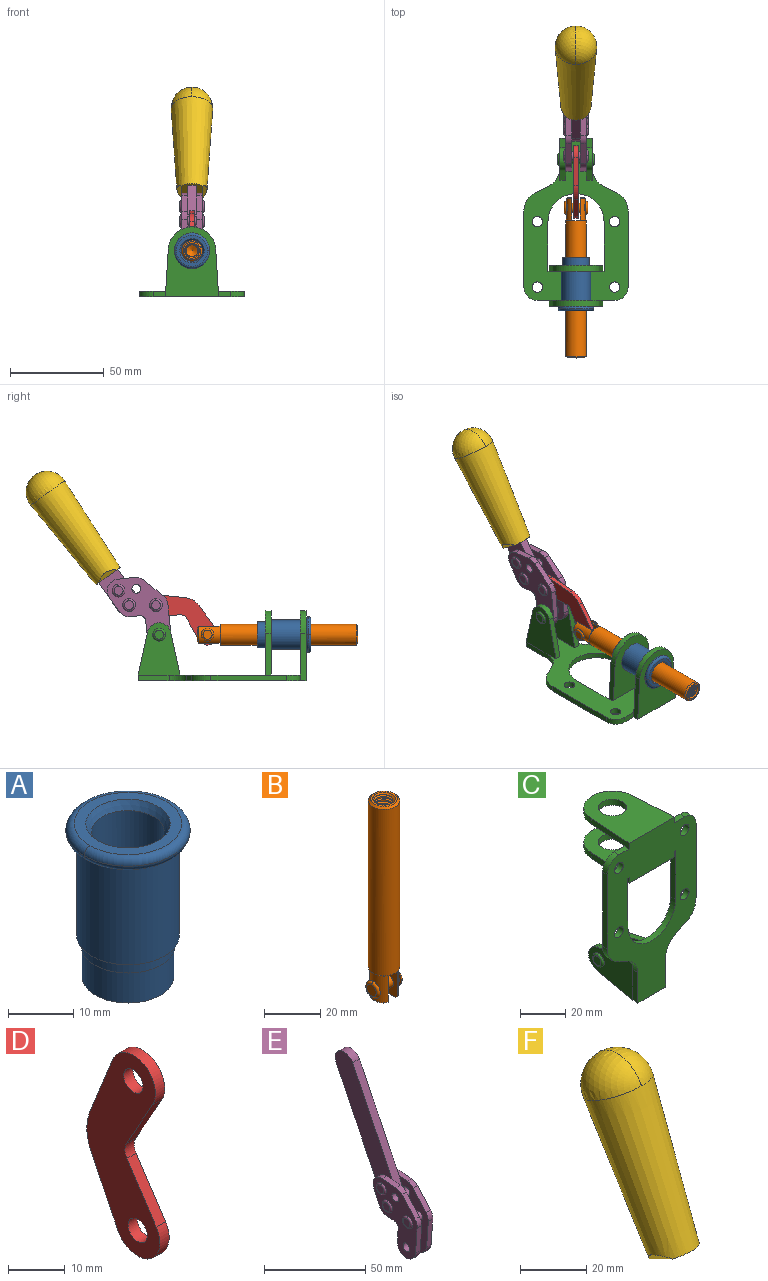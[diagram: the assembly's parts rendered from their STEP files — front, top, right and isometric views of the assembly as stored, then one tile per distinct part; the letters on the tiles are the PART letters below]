
ASSEMBLY  parts=6 mates=6
PART A: 15 faces, bbox 20.6x20.6x28.7 mm
  f0: torus R=8.26mm, axis (0,0,1), area 56.8mm2, adj f1,f10,f12
  f1: torus R=8.26mm, axis (0,0,1), area 56.8mm2, adj f0,f6,f13
  f2: cylinder r=5.59mm len=25.91mm, axis (0,0,1), area 909.6mm2, adj f3,f4
  f3: cone r=6.86mm half-angle=45deg, axis (0,0,-1), area 70.2mm2, adj f2,f14
  f4: cone r=6.47mm half-angle=30deg, axis (0,0,1), area 66.7mm2, adj f2,f13
  f5: cylinder r=7.04mm len=14.07mm, axis (0,0,1), area 252.6mm2, adj f11,f14
  f6: torus R=8.26mm, axis (0,0,1), area 56.8mm2, adj f1,f12,f13
  f7: cylinder r=7.16mm len=14.33mm, axis (0,0,1), area 91.5mm2, adj f9,f11
  f8: cylinder r=7.86mm len=18.42mm, axis (0,0,1), area 909.6mm2, adj f9,f10
  f9: plane 15.72x15.72mm, normal (0,0,-1), area 33mm2, adj f7,f8
  f10: plane 16.51x16.51mm, normal (0,0,-1), area 19.9mm2, adj f0,f8,f12
  f11: plane 14.33x14.33mm, normal (0,0,-1), area 5.7mm2, adj f5,f7
  f12: torus R=8.26mm, axis (0,0,1), area 56.8mm2, adj f0,f6,f10
  f13: plane 16.51x16.51mm, normal (0,0,1), area 82.7mm2, adj f1,f4,f6
  f14: plane 14.07x14.07mm, normal (0,0,-1), area 7.8mm2, adj f3,f5
PART B: 48 faces, bbox 12.6x11.1x86.1 mm
  f0: torus R=2.41mm, axis (-1,0,0), area 15mm2, adj f30,f32,f34
  f1: torus R=2.41mm, axis (-1,0,0), area 15mm2, adj f29,f31,f33
  f2: cylinder r=5.54mm len=72.39mm, axis (0,0,1), area 2518.5mm2, adj f3,f4,f42,f43
  f3: cone r=5.54mm half-angle=45deg, axis (0,0,1), area 7.6mm2, adj f2,f5,f41
  f4: cone r=5.54mm half-angle=45deg, axis (0,0,-1), area 34.9mm2, adj f2,f39
  f5: cylinder r=5.08mm len=11.48mm, axis (0,0,1), area 108.3mm2, adj f3,f7,f8,f41
  f6: cylinder r=2.41mm len=4.83mm, axis (-1,0,0), area 71.2mm2, adj f40,f41
  f7: cylinder r=2.41mm len=4.83mm, axis (-1,0,0), area 7.6mm2, adj f5,f34
  f8: cone r=5.08mm half-angle=45deg, axis (0,0,1), area 10.6mm2, adj f5,f37,f41
  f9: cone r=3.98mm half-angle=45deg, axis (0,0,1), area 17.6mm2, adj f27,f39,f45,f46,f47
  f10: cylinder r=2.41mm len=4.83mm, axis (-1,0,0), area 7.6mm2, adj f33,f38
  f11: cylinder r=3.2mm len=6.4mm, axis (0,0,1), area 78.4mm2, adj f12,f28,f44,f45,f47
  f12: cylinder r=3.2mm len=6.4mm, axis (0,0,1), area 10.5mm2, adj f11,f13,f45,f47
  f13: cylinder r=3.2mm len=6.4mm, axis (0,0,1), area 10.5mm2, adj f12,f14,f45,f47
  f14: cylinder r=3.2mm len=6.4mm, axis (0,0,1), area 10.5mm2, adj f13,f15,f45,f47
  f15: cylinder r=3.2mm len=6.4mm, axis (0,0,1), area 10.5mm2, adj f14,f16,f45,f47
  f16: cylinder r=3.2mm len=6.4mm, axis (0,0,1), area 10.5mm2, adj f15,f17,f45,f47
  f17: cylinder r=3.2mm len=6.4mm, axis (0,0,1), area 10.5mm2, adj f16,f18,f45,f47
  f18: cylinder r=3.2mm len=6.4mm, axis (0,0,1), area 10.5mm2, adj f17,f19,f45,f47
  f19: cylinder r=3.2mm len=6.4mm, axis (0,0,1), area 10.5mm2, adj f18,f20,f45,f47
  f20: cylinder r=3.2mm len=6.4mm, axis (0,0,1), area 10.5mm2, adj f19,f21,f45,f47
  f21: cylinder r=3.2mm len=6.4mm, axis (0,0,1), area 10.5mm2, adj f20,f22,f45,f47
  f22: cylinder r=3.2mm len=6.4mm, axis (0,0,1), area 10.5mm2, adj f21,f23,f45,f47
  f23: cylinder r=3.2mm len=6.4mm, axis (0,0,1), area 10.5mm2, adj f22,f24,f45,f47
  f24: cylinder r=3.2mm len=6.4mm, axis (0,0,1), area 10.5mm2, adj f23,f25,f45,f47
  f25: cylinder r=3.2mm len=6.4mm, axis (0,0,1), area 10.5mm2, adj f24,f26,f45,f47
  f26: cylinder r=3.2mm len=6.4mm, axis (0,0,1), area 10.5mm2, adj f25,f27,f45,f47
  f27: cylinder r=3.2mm len=6.4mm, axis (0,0,1), area 7.4mm2, adj f9,f26,f45,f47
  f28: cone r=3.2mm half-angle=60deg, axis (0,0,1), area 37.2mm2, adj f11
  f29: plane 4.83x4.83mm, normal (-1,0,0), area 18.3mm2, adj f1,f31
  f30: plane 4.83x4.83mm, normal (1,0,0), area 18.3mm2, adj f0,f32
  f31: torus R=2.41mm, axis (-1,0,0), area 15mm2, adj f1,f29,f33
  f32: torus R=2.41mm, axis (-1,0,0), area 15mm2, adj f0,f30,f34
  f33: plane 6.83x6.83mm, normal (1,0,0), area 18.3mm2, adj f1,f10,f31
  f34: plane 6.83x6.83mm, normal (-1,0,0), area 18.3mm2, adj f0,f7,f32
  f35: cone r=5.08mm half-angle=45deg, axis (0,0,1), area 10.6mm2, adj f36,f38,f40
  f36: plane 7.25x1.97mm, normal (0,0,-1), area 10mm2, adj f35,f40
  f37: plane 7.25x1.97mm, normal (0,0,-1), area 10mm2, adj f8,f41
  f38: cylinder r=5.08mm len=11.48mm, axis (0,0,1), area 108.3mm2, adj f10,f35,f40,f42
  f39: plane 9.55x9.55mm, normal (0,0,1), area 22mm2, adj f4,f9
  f40: plane 12.76x10.09mm, normal (1,0,0), area 95.7mm2, adj f6,f35,f36,f38,f42,f43
  f41: plane 12.76x10.09mm, normal (-1,0,0), area 95.7mm2, adj f3,f5,f6,f8,f37,f43
  f42: cone r=5.54mm half-angle=45deg, axis (0,0,1), area 7.6mm2, adj f2,f38,f40
  f43: plane 11.07x4.7mm, normal (0,0,-1), area 50.4mm2, adj f2,f40,f41
  f44: plane 0.89x0.62mm, normal (-1,0,0), area 0.3mm2, adj f11,f45,f46,f47
  f45: bspline ~24.8x7.63mm, area 266.6mm2, adj f9,f11,f12,f13,f14,f15,f16,f17
  f46: bspline ~24.87x7.63mm, area 73.6mm2, adj f9,f44,f45,f47
  f47: bspline ~24.98x7.63mm, area 272.5mm2, adj f9,f11,f12,f13,f14,f15,f16,f17
PART C: 55 faces, bbox 55.7x37.4x89.8 mm
  f0: torus R=2.41mm, axis (-1,0,0), area 15mm2, adj f11,f15,f25
  f1: torus R=2.41mm, axis (-1,0,0), area 15mm2, adj f10,f12,f22
  f2: cylinder r=2.78mm len=5.56mm, axis (0,-1,0), area 54.2mm2, adj f30,f54
  f3: cylinder r=14.99mm len=29.97mm, axis (0,-1,0), area 145.9mm2, adj f30,f49,f53,f54
  f4: cylinder r=2.78mm len=5.56mm, axis (0,-1,0), area 54.2mm2, adj f30,f54
  f5: cylinder r=2.78mm len=5.56mm, axis (0,-1,0), area 54.2mm2, adj f30,f54
  f6: cylinder r=2.78mm len=5.56mm, axis (0,-1,0), area 54.2mm2, adj f30,f54
  f7: cylinder r=6.35mm len=12.7mm, axis (0,0,1), area 123.6mm2, adj f27,f51
  f8: cylinder r=6.35mm len=12.7mm, axis (0,0,-1), area 124.7mm2, adj f21,f35
  f9: cylinder r=2.41mm len=11.18mm, axis (-1,0,0), area 169.4mm2, adj f16,f19
  f10: plane 4.83x4.83mm, normal (1,0,0), area 18.3mm2, adj f1,f12
  f11: plane 4.83x4.83mm, normal (-1,0,0), area 18.3mm2, adj f0,f15
  f12: torus R=2.41mm, axis (-1,0,0), area 15mm2, adj f1,f10,f22
  f13: cylinder r=6.35mm len=12.41mm, axis (1,0,0), area 53.4mm2, adj f18,f19,f22,f23
  f14: cylinder r=6.35mm len=12.41mm, axis (-1,0,0), area 53.4mm2, adj f16,f17,f24,f25
  f15: torus R=2.41mm, axis (-1,0,0), area 15mm2, adj f0,f11,f25
  f16: plane 27.86x22.35mm, normal (1,0,0), area 425.4mm2, adj f9,f14,f17,f24,f30
  f17: plane 22.86x4.97mm, normal (0,0.21,0.98), area 72.5mm2, adj f14,f16,f25,f30
  f18: plane 22.86x4.97mm, normal (0,0.21,0.98), area 72.5mm2, adj f13,f19,f22,f30
  f19: plane 27.86x22.35mm, normal (-1,0,0), area 425.4mm2, adj f9,f13,f18,f23,f30
  f20: cylinder r=12.7mm len=25.35mm, axis (0,0,-1), area 119.8mm2, adj f21,f34,f35,f36
  f21: plane 34.21x28.07mm, normal (0,0,-1), area 702.4mm2, adj f8,f20,f30,f34,f36
  f22: plane 27.96x22.45mm, normal (1,0,0), area 407.2mm2, adj f1,f12,f13,f18,f23,f30,f42,f43
  f23: plane 22.86x4.97mm, normal (0,0.21,-0.98), area 72.5mm2, adj f13,f19,f22,f44
  f24: plane 22.86x4.97mm, normal (0,0.21,-0.98), area 72.5mm2, adj f14,f16,f25,f44
  f25: plane 27.86x22.35mm, normal (-1,0,0), area 407.1mm2, adj f0,f14,f15,f17,f24,f30,f45,f46
  f26: plane 3.1x0.95mm, normal (0,0,-1), area 2.7mm2, adj f30,f49,f50,f54
  f27: plane 34.21x28.07mm, normal (0,0,1), area 702.4mm2, adj f7,f28,f30,f50,f52
  f28: cylinder r=12.7mm len=25.35mm, axis (0,0,1), area 118.8mm2, adj f27,f50,f51,f52
  f29: plane 3.1x0.95mm, normal (0,0,-1), area 2.7mm2, adj f30,f52,f53,f54
  f30: plane 86.54x55.63mm, normal (0,1,0), area 2362.9mm2, adj f2,f3,f4,f5,f6,f16,f17,f18
  f31: plane 40.56x3.1mm, normal (-1,0,0), area 125.7mm2, adj f30,f32,f48,f54
  f32: cylinder r=7.11mm len=7.11mm, axis (0,-1,0), area 34.6mm2, adj f30,f31,f33,f54
  f33: plane 6.67x3.1mm, normal (0,0,1), area 20.4mm2, adj f30,f32,f34,f54
  f34: plane 25.39x3.13mm, normal (-1,0.06,0), area 79.5mm2, adj f20,f21,f33,f35,f54
  f35: plane 37.31x28.45mm, normal (0,0,1), area 789.9mm2, adj f8,f20,f34,f36,f54
  f36: plane 25.39x3.13mm, normal (1,0.06,0), area 79.5mm2, adj f20,f21,f35,f37,f54
  f37: plane 6.67x3.1mm, normal (0,0,1), area 20.4mm2, adj f30,f36,f38,f54
  f38: cylinder r=7.11mm len=7.11mm, axis (0,-1,0), area 34.6mm2, adj f30,f37,f39,f54
  f39: plane 40.56x3.1mm, normal (1,0,0), area 125.7mm2, adj f30,f38,f40,f54
  f40: cylinder r=11.18mm len=10.16mm, axis (0,-1,0), area 39.5mm2, adj f30,f39,f41,f54
  f41: plane 6.09x3.1mm, normal (0.42,0,-0.91), area 20.8mm2, adj f30,f40,f42,f54
  f42: cylinder r=11.18mm len=9.41mm, axis (0,-1,0), area 37.2mm2, adj f22,f30,f41,f43,f54
  f43: plane 16.5x3.1mm, normal (1,0,0), area 51.1mm2, adj f22,f42,f44,f54
  f44: plane 17.37x3.1mm, normal (0,0,-1), area 53.8mm2, adj f23,f24,f30,f43,f45,f54
  f45: plane 16.5x3.1mm, normal (-1,0,0), area 51.1mm2, adj f25,f44,f46,f54
  f46: cylinder r=11.18mm len=9.41mm, axis (0,-1,0), area 37.2mm2, adj f25,f30,f45,f47,f54
  f47: plane 6.09x3.1mm, normal (-0.42,0,-0.91), area 20.8mm2, adj f30,f46,f48,f54
  f48: cylinder r=11.18mm len=10.16mm, axis (0,-1,0), area 39.5mm2, adj f30,f31,f47,f54
  f49: plane 26.54x3.1mm, normal (-1,0,0), area 82.3mm2, adj f3,f26,f30,f54
  f50: plane 25.39x3.1mm, normal (1,0.06,0), area 78.8mm2, adj f26,f27,f28,f51,f54
  f51: plane 37.31x28.45mm, normal (0,0,-1), area 789.9mm2, adj f7,f28,f50,f52,f54
  f52: plane 25.39x3.1mm, normal (-1,0.06,0), area 78.8mm2, adj f27,f28,f29,f51,f54
  f53: plane 26.54x3.1mm, normal (1,0,0), area 82.3mm2, adj f3,f29,f30,f54
  f54: plane 89.66x55.63mm, normal (0,-1,0), area 2678.5mm2, adj f2,f3,f4,f5,f6,f26,f29,f31
PART D: 12 faces, bbox 2.3x18.2x42.8 mm
  f0: cylinder r=2.4mm len=4.8mm, axis (1,0,0), area 34.9mm2, adj f4,f11
  f1: cylinder r=10.41mm len=8.47mm, axis (1,0,0), area 20.2mm2, adj f4,f9,f10,f11
  f2: cylinder r=3.05mm len=3.16mm, axis (1,0,0), area 7.7mm2, adj f4,f6,f7,f11
  f3: cylinder r=2.4mm len=4.8mm, axis (1,0,0), area 34.9mm2, adj f4,f11
  f4: plane 42.81x18.23mm, normal (-1,0,0), area 414.1mm2, adj f0,f1,f2,f3,f5,f6,f7,f8
  f5: cylinder r=5.54mm len=10.67mm, axis (1,0,0), area 41.8mm2, adj f4,f6,f10,f11
  f6: plane 11.66x6.53mm, normal (0,-0.87,-0.49), area 30.9mm2, adj f2,f4,f5,f11
  f7: plane 11.17x7.33mm, normal (0,-0.84,0.55), area 30.9mm2, adj f2,f4,f8,f11
  f8: cylinder r=5.54mm len=10.51mm, axis (1,0,0), area 41.8mm2, adj f4,f7,f9,f11
  f9: plane 13.67x6.67mm, normal (0,0.9,-0.44), area 35.1mm2, adj f1,f4,f8,f11
  f10: plane 14.1x5.7mm, normal (0,0.93,0.37), area 35.1mm2, adj f1,f4,f5,f11
  f11: plane 42.81x18.23mm, normal (1,0,0), area 414.1mm2, adj f0,f1,f2,f3,f5,f6,f7,f8
PART E: 59 faces, bbox 12.9x60.2x99.6 mm
  f0: torus R=2.39mm, axis (-1,0,0), area 14.9mm2, adj f20,f43,f51
  f1: torus R=2.39mm, axis (-1,0,0), area 14.9mm2, adj f19,f42,f51
  f2: torus R=2.39mm, axis (-1,0,0), area 14.9mm2, adj f18,f35,f51
  f3: torus R=2.39mm, axis (-1,0,0), area 14.9mm2, adj f14,f17,f23
  f4: torus R=2.39mm, axis (-1,0,0), area 14.9mm2, adj f13,f16,f23
  f5: torus R=2.39mm, axis (-1,0,0), area 14.9mm2, adj f12,f15,f23
  f6: cylinder r=2.39mm len=4.78mm, axis (1,0,0), area 46.5mm2, adj f48,f50,f51
  f7: cylinder r=2.39mm len=4.78mm, axis (1,0,0), area 46.5mm2, adj f50,f51
  f8: cylinder r=6.35mm len=12.68mm, axis (1,0,0), area 61.8mm2, adj f38,f39,f50,f51
  f9: cylinder r=2.39mm len=4.78mm, axis (-1,0,0), area 70.5mm2, adj f46,f50
  f10: cylinder r=2.39mm len=4.78mm, axis (-1,0,0), area 46.5mm2, adj f23,f45,f46
  f11: cylinder r=2.39mm len=4.78mm, axis (-1,0,0), area 46.5mm2, adj f23,f46
  f12: plane 4.78x4.78mm, normal (1,0,0), area 17.9mm2, adj f5,f15
  f13: plane 4.78x4.78mm, normal (1,0,0), area 17.9mm2, adj f4,f16
  f14: plane 4.78x4.78mm, normal (1,0,0), area 17.9mm2, adj f3,f17
  f15: torus R=2.39mm, axis (-1,0,0), area 14.9mm2, adj f5,f12,f23
  f16: torus R=2.39mm, axis (-1,0,0), area 14.9mm2, adj f4,f13,f23
  f17: torus R=2.39mm, axis (-1,0,0), area 14.9mm2, adj f3,f14,f23
  f18: plane 4.78x4.78mm, normal (-1,0,0), area 17.9mm2, adj f2,f35
  f19: plane 4.78x4.78mm, normal (-1,0,0), area 17.9mm2, adj f1,f42
  f20: plane 4.78x4.78mm, normal (-1,0,0), area 17.9mm2, adj f0,f43
  f21: plane 2.26x0.2mm, normal (1,0,0), area 0.2mm2, adj f31,f44
  f22: plane 2.26x0.2mm, normal (-1,0,0), area 0.2mm2, adj f41,f44
  f23: plane 39.37x30.77mm, normal (1,0,0), area 565.5mm2, adj f3,f4,f5,f10,f11,f15,f16,f17
  f24: cylinder r=6.1mm len=4.15mm, axis (-1,0,0), area 14.7mm2, adj f23,f25,f32,f46
  f25: plane 10.25x9.01mm, normal (0,-0.75,0.66), area 42.3mm2, adj f23,f24,f26,f46
  f26: cylinder r=6.35mm len=4.64mm, axis (-1,0,0), area 15.6mm2, adj f23,f25,f27,f46
  f27: plane 15.84x3.1mm, normal (0,-1,-0.07), area 49.2mm2, adj f23,f26,f28,f46
  f28: cylinder r=6.35mm len=12.68mm, axis (-1,0,0), area 61.8mm2, adj f23,f27,f29,f46
  f29: plane 8.11x3.1mm, normal (0,1,0.07), area 25.2mm2, adj f23,f28,f30,f46
  f30: cylinder r=3.05mm len=3.25mm, axis (-1,0,0), area 14.8mm2, adj f23,f29,f31,f46
  f31: plane 5.99x3.1mm, normal (0,0.07,-1), area 18.6mm2, adj f21,f23,f30,f44,f46
  f32: plane 9.5x3.1mm, normal (0,-0.07,1), area 29.5mm2, adj f23,f24,f33,f46,f47
  f33: cylinder r=6.1mm len=8.63mm, axis (-1,0,0), area 39.1mm2, adj f23,f32,f34,f47
  f34: plane 8.65x3.96mm, normal (0,0.91,-0.42), area 29.5mm2, adj f23,f33,f44,f47
  f35: torus R=2.39mm, axis (-1,0,0), area 14.9mm2, adj f2,f18,f51
  f36: plane 10.25x9.01mm, normal (0,-0.75,0.66), area 42.3mm2, adj f37,f49,f50,f51
  f37: cylinder r=6.35mm len=4.64mm, axis (1,0,0), area 15.6mm2, adj f36,f38,f50,f51
  f38: plane 15.84x3.1mm, normal (0,-1,-0.07), area 49.2mm2, adj f8,f37,f50,f51
  f39: plane 8.11x3.1mm, normal (0,1,0.07), area 25.2mm2, adj f8,f40,f50,f51
  f40: cylinder r=3.05mm len=3.25mm, axis (1,0,0), area 14.8mm2, adj f39,f41,f50,f51
  f41: plane 5.99x3.1mm, normal (0,0.07,-1), area 18.6mm2, adj f22,f40,f44,f50,f51
  f42: torus R=2.39mm, axis (-1,0,0), area 14.9mm2, adj f1,f19,f51
  f43: torus R=2.39mm, axis (-1,0,0), area 14.9mm2, adj f0,f20,f51
  f44: cylinder r=6.35mm len=12.12mm, axis (-1,0,0), area 128.9mm2, adj f21,f22,f23,f31,f34,f41,f46,f47
  f45: plane 2.65x1.35mm, normal (1,0,0), area 1mm2, adj f10,f55
  f46: plane 39.08x20.42mm, normal (-1,0,0), area 412.5mm2, adj f9,f10,f11,f24,f25,f26,f27,f28
  f47: plane 77.62x39.82mm, normal (1,0,0), area 850mm2, adj f32,f33,f34,f44,f53,f54,f55
  f48: plane 2.65x1.35mm, normal (-1,0,0), area 1mm2, adj f6,f55
  f49: cylinder r=6.1mm len=4.15mm, axis (1,0,0), area 14.7mm2, adj f36,f50,f51,f56
  f50: plane 39.08x20.42mm, normal (1,0,0), area 412.5mm2, adj f6,f7,f8,f9,f36,f37,f38,f39
  f51: plane 39.37x30.77mm, normal (-1,0,0), area 565.5mm2, adj f0,f1,f2,f6,f7,f8,f35,f36
  f52: plane 8.65x3.96mm, normal (0,0.91,-0.42), area 29.5mm2, adj f44,f51,f57,f58
  f53: plane 68.49x33.4mm, normal (0,0.9,-0.44), area 358.1mm2, adj f44,f47,f54,f58
  f54: cylinder r=6.35mm len=12.06mm, axis (1,0,0), area 93.7mm2, adj f47,f53,f55,f58
  f55: plane 68.49x33.4mm, normal (0,-0.9,0.44), area 358.1mm2, adj f44,f45,f46,f47,f48,f50,f54,f58
  f56: plane 9.5x3.1mm, normal (0,-0.07,1), area 29.5mm2, adj f49,f50,f51,f57,f58
  f57: cylinder r=6.1mm len=8.63mm, axis (1,0,0), area 39.1mm2, adj f51,f52,f56,f58
  f58: plane 77.62x39.82mm, normal (-1,0,0), area 850mm2, adj f44,f52,f53,f54,f55,f56,f57
PART F: 11 faces, bbox 22.3x42.6x64.5 mm
  f0: sphere r=11.13mm, area 411.4mm2, adj f1,f8
  f1: cone r=11.11mm half-angle=3.3deg, axis (0,0.44,0.9), area 3251.8mm2, adj f0,f7,f8,f9,f10
  f2: cylinder r=6.16mm len=11.7mm, axis (1,0,0), area 89.5mm2, adj f3,f4,f5,f6
  f3: plane 60.23x36.75mm, normal (-1,0,0), area 763.6mm2, adj f2,f4,f6,f10
  f4: plane 51.37x25.05mm, normal (0,0.9,-0.44), area 264.2mm2, adj f2,f3,f5,f10
  f5: plane 60.23x36.75mm, normal (1,0,0), area 763.6mm2, adj f2,f4,f6,f10
  f6: plane 51.37x25.05mm, normal (0,-0.9,0.44), area 264.2mm2, adj f2,f3,f5,f10
  f7: plane 9.95x5.95mm, normal (0.71,-0.31,-0.64), area 25.8mm2, adj f1,f10
  f8: sphere r=11.13mm, area 411.4mm2, adj f0,f1
  f9: plane 9.95x5.95mm, normal (-0.71,-0.31,-0.64), area 25.8mm2, adj f1,f10
  f10: plane 14.27x11.38mm, normal (0,-0.44,-0.9), area 106.7mm2, adj f1,f3,f4,f5,f6,f7,f9
PLACE A rot(axis=(1,0,0),90deg) t=(0,9.43,0)mm
PLACE B rot(axis=(1,0,0),90deg) t=(0,31.11,0)mm
PLACE C rot(axis=(1,0,0),90deg) t=(0,9.43,0)mm fixed
PLACE D rot(axis=(1,0,0),121.8deg) t=(0,41.76,11.86)mm
PLACE E rot(axis=(-1,0,0),10deg) t=(0,22.86,60.49)mm
PLACE F rot(axis=(-1,0,0),10deg) t=(-0.04,22.86,60.49)mm
MATE slider B.f2 <-> A.f2  axis (0,-1,0) through (0,-27.67,24.61)mm
MATE revolute C.f0 <-> E.f7  axis (-1,0,0) through (0,41.52,24.61)mm
MATE revolute E.f4 <-> D.f3  axis (-1,0,0) through (0,43.18,40.4)mm
MATE fastened F.f2 <-> E.f54  axis (1,0,0) through (-2.35,102.33,102.1)mm
MATE revolute D.f5 <-> B.f6  axis (1,0,0) through (0,15.64,24.61)mm
MATE fastened C.f7 <-> A.f2  axis (0,1,0) through (0,-36.96,24.61)mm
